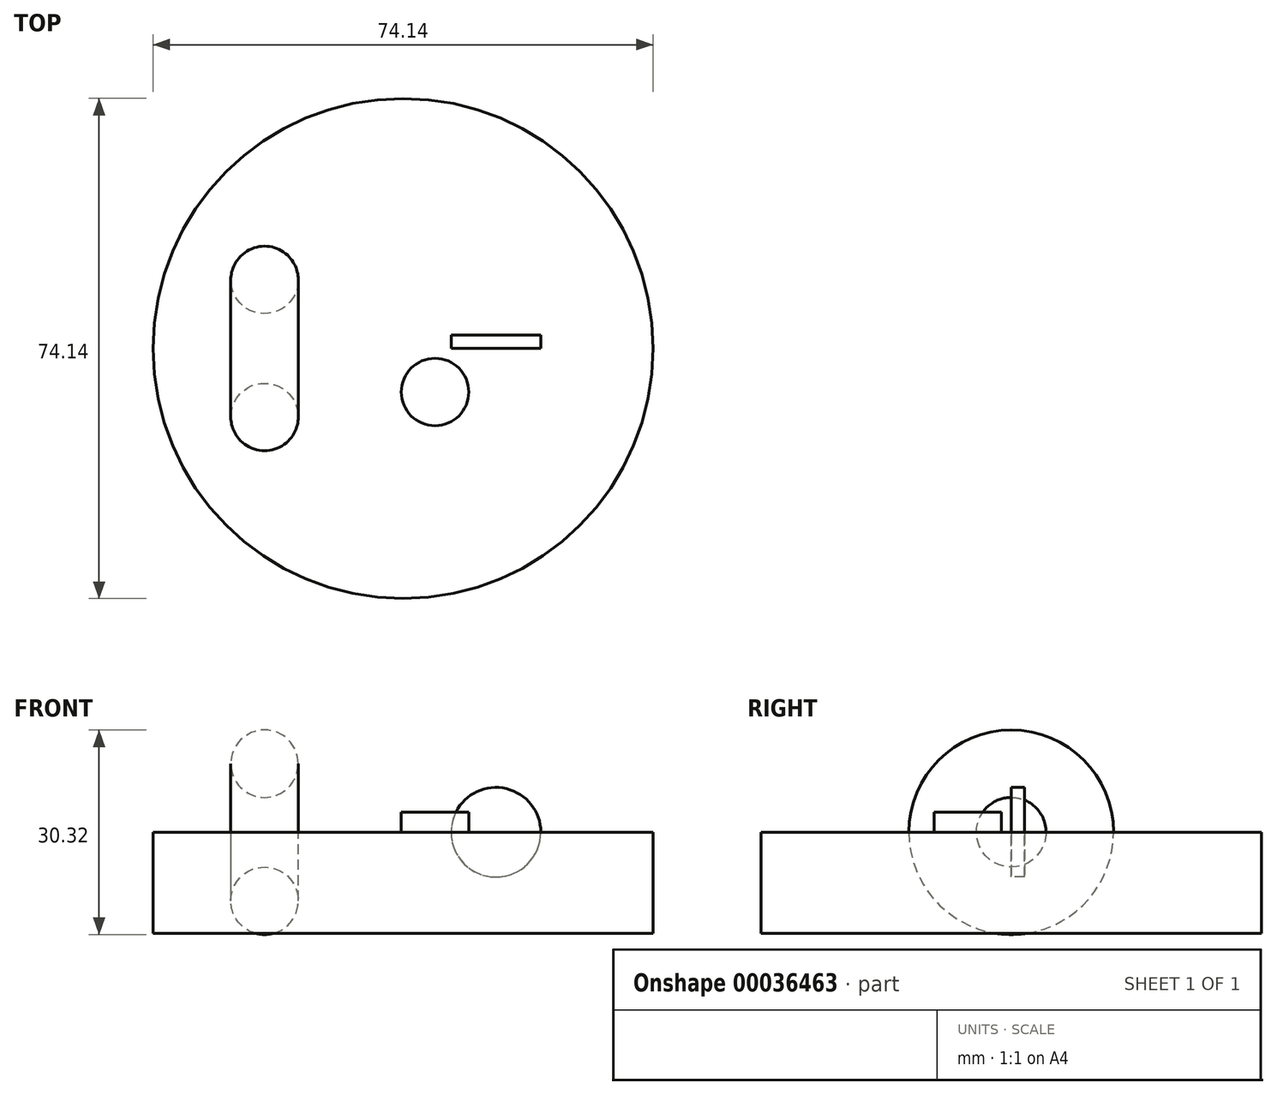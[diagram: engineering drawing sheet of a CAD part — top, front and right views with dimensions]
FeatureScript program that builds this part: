
annotation { "Feature Type Name" : "Feature", "Feature Type Description" : "" }
export const myFeature = defineFeature(function(context is Context, id is Id, definition is map)
    precondition{}
    {
        {
            var Q0;
            Q0=qCreatedBy(makeId("Front.planeOp"),FACE);
            var sketch = newSketch(context, id + "F0", { "sketchPlane" : qUnion([Q0])});
            skCircle(sketch, "E0", {"center": v(-20.53, 10.16) * mm, "radius": 5 * mm});
            skLineSegment(sketch, "E1", {"start": v(-29.39, 0) * mm, "end": v(-8.45, 0) * mm});
            skSolve(sketch);
        }
        {
            var Q0;
            Q0=makeQuery(id+"F0.imprint","IMPRINT",FACE,{"disambiguationData":[TD([[makeQuery(id+"F0.imprint","IMPRINT",EDGE,{"derivedFrom":sQuery(id+"F0.wireOp",EDGE,"E0")}),1.0]])]});
            var Q1;
            Q1=sQuery(id+"F0.wireOp",EDGE,"E1");
            revolve(context, id + "F1", {"entities" : qUnion([Q0]), "axis" : qUnion([Q1]), "revolveType" : RevolveType.FULL});
        }
        {
            var Q0;
            Q0=qCreatedBy(makeId("Top.planeOp"),FACE);
            var sketch = newSketch(context, id + "F2", { "sketchPlane" : qUnion([Q0])});
            skCircle(sketch, "E2", {"center": v(0, 0) * mm, "radius": 5 * mm});
            skCircle(sketch, "E3", {"center": v(4.74, -6.46) * mm, "radius": 5 * mm});
            skSolve(sketch);
        }
        {
            var Q0;
            Q0=makeQuery(id+"F2.imprint","IMPRINT",FACE,{"disambiguationData":[TD([[makeQuery(id+"F2.imprint","IMPRINT",EDGE,{"derivedFrom":sQuery(id+"F2.wireOp",EDGE,"E3")}),1.0]])]});
            extrude(context, id + "F3", {"entities" : qUnion([Q0]), "depth" : 3 * mm});
        }
        {
            var Q0;
            Q0=qCreatedBy(makeId("Top.planeOp"),FACE);
            var sketch = newSketch(context, id + "F4", { "sketchPlane" : qUnion([Q0])});
            skCircle(sketch, "E4", {"center": v(0, 0) * mm, "radius": 37.07 * mm});
            skSolve(sketch);
        }
        {
            var Q0;
            Q0=qCreatedBy(makeId("Front.planeOp"),FACE);
            var sketch = newSketch(context, id + "F5", { "sketchPlane" : qUnion([Q0])});
            skCircle(sketch, "E5", {"center": v(13.77, 0) * mm, "radius": 6.64 * mm});
            skSolve(sketch);
        }
        {
            var Q0;
            Q0 = qSketchRegion(id + "F5", true);
            extrude(context, id + "F6", {"entities" : qUnion([Q0]), "oppositeDirection" : true, "depth" : 2 * mm});
        }
        {
            var Q0;
            Q0=makeQuery(id+"F4.imprint","IMPRINT",FACE,{"disambiguationData":[TD([[makeQuery(id+"F4.imprint","IMPRINT",EDGE,{"derivedFrom":sQuery(id+"F4.wireOp",EDGE,"E4")}),1.0]])]});
            extrude(context, id + "F7", {"entities" : qUnion([Q0]), "oppositeDirection" : true, "depth" : 15 * mm});
        }
    });
